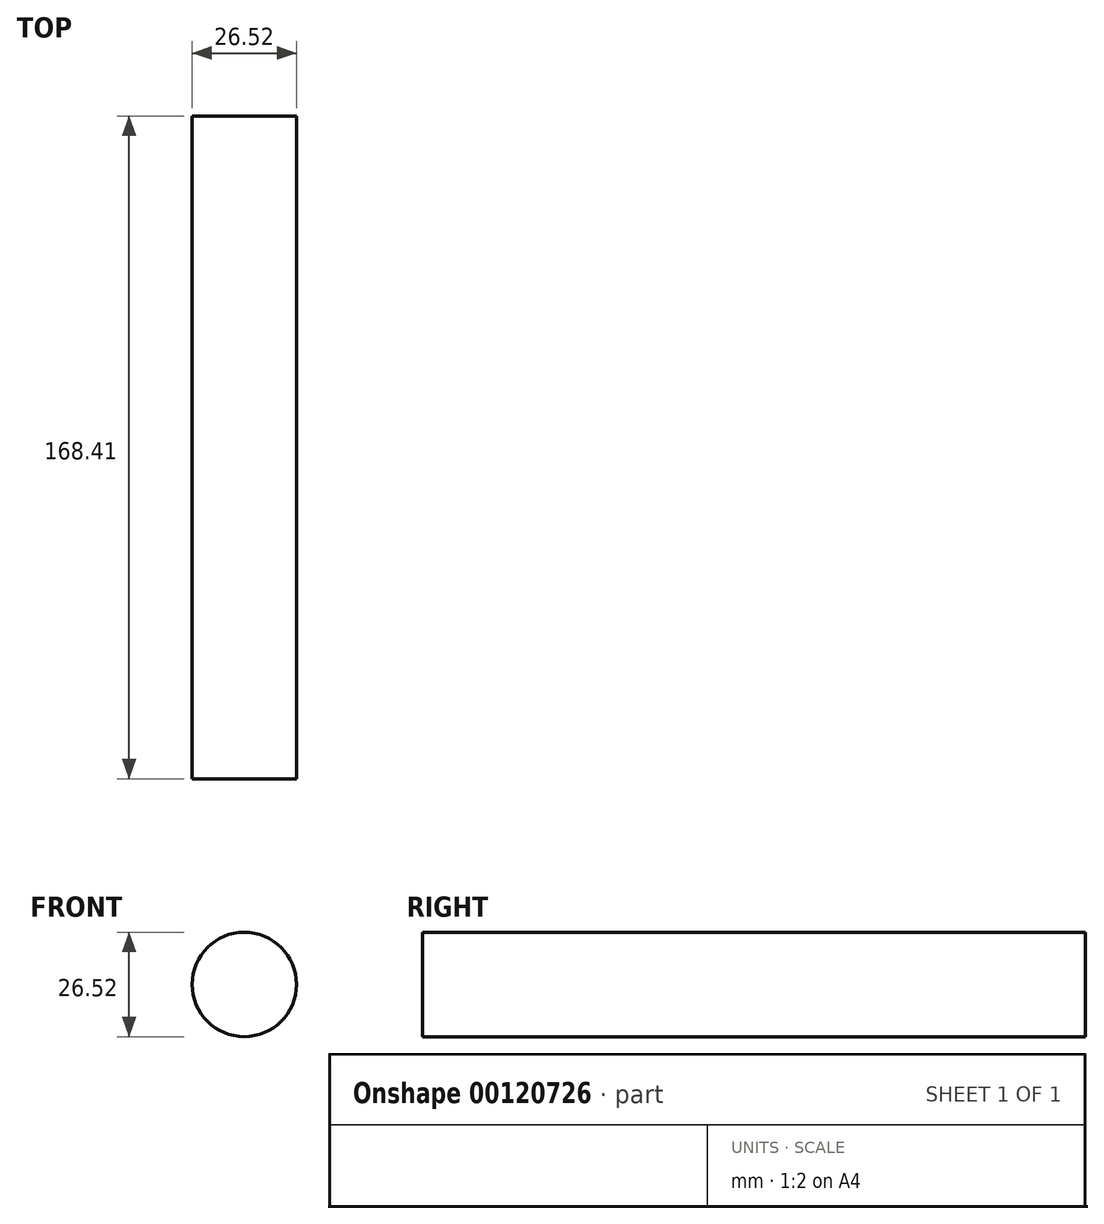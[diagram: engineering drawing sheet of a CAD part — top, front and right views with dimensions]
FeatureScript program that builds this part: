
annotation { "Feature Type Name" : "Feature", "Feature Type Description" : "" }
export const myFeature = defineFeature(function(context is Context, id is Id, definition is map)
    precondition{}
    {
        {
            var Q0;
            Q0=qCreatedBy(makeId("Front.planeOp"),FACE);
            var sketch = newSketch(context, id + "F0", { "sketchPlane" : qUnion([Q0])});
            skCircle(sketch, "E0", {"center": v(0, 0) * mm, "radius": 13.26 * mm});
            skSolve(sketch);
        }
        {
            var Q0;
            Q0=sQuery(id+"F0.wireOp",EDGE,"E0");
            extrude(context, id + "F1", {"bodyType" : ToolBodyType.SURFACE, "surfaceEntities" : qUnion([Q0]), "depth" : 168.4 * mm});
        }
    });
